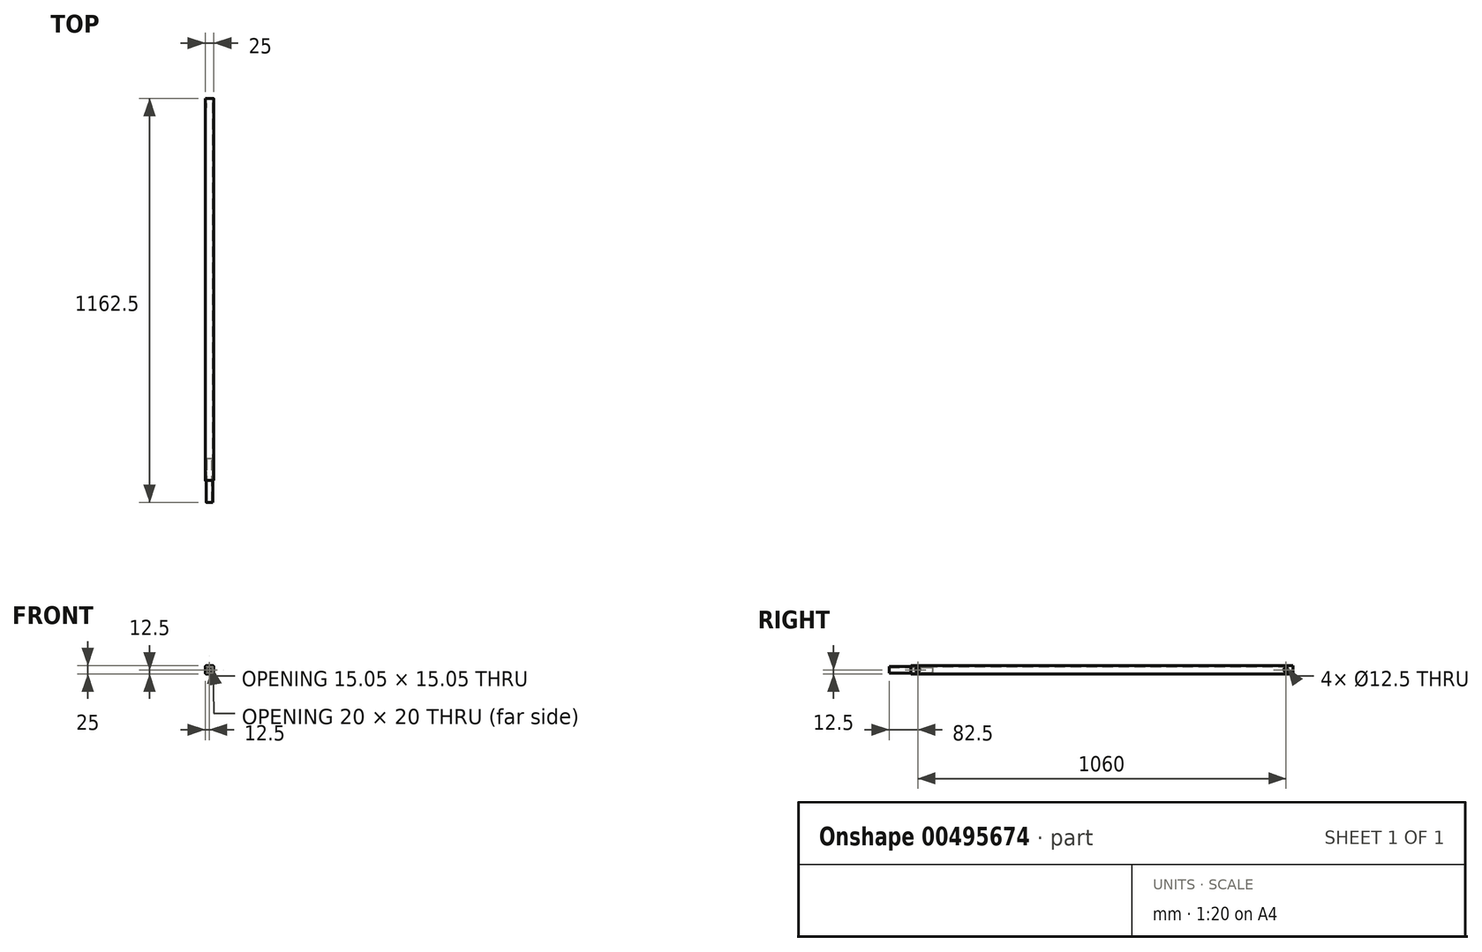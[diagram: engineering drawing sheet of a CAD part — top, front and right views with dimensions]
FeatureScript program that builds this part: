
annotation { "Feature Type Name" : "Feature", "Feature Type Description" : "" }
export const myFeature = defineFeature(function(context is Context, id is Id, definition is map)
    precondition{}
    {
        {
            var Q0;
            Q0=qCreatedBy(makeId("Front.planeOp"),FACE);
            var sketch = newSketch(context, id + "F0", { "sketchPlane" : qUnion([Q0])});
            skLineSegment(sketch, "E0.bottom", {"start": v(7.5, 12.5) * mm, "end": v(-7.5, 12.5) * mm});
            skLineSegment(sketch, "E0.top", {"start": v(7.5, -12.5) * mm, "end": v(-7.5, -12.5) * mm});
            skLineSegment(sketch, "E0.left", {"start": v(12.5, 7.5) * mm, "end": v(12.5, -7.5) * mm});
            skLineSegment(sketch, "E0.right", {"start": v(-12.5, 7.5) * mm, "end": v(-12.5, -7.5) * mm});
            skPoint(sketch, "E0.middle", {"position": v(0, 0) * mm});
            skPoint(sketch, "E1.visualSharp", {"position": v(-12.5, 12.5) * mm});
            skArc(sketch, "E1.filletArc", {"start": v(-7.5, 12.5) * mm, "mid": v(-11.04, 11.04) * mm, "end": v(-12.5, 7.5) * mm});
            skPoint(sketch, "E2.visualSharp", {"position": v(12.5, 12.5) * mm});
            skArc(sketch, "E2.filletArc", {"start": v(12.5, 7.5) * mm, "mid": v(11.04, 11.04) * mm, "end": v(7.5, 12.5) * mm});
            skPoint(sketch, "E3.visualSharp", {"position": v(12.5, -12.5) * mm});
            skArc(sketch, "E3.filletArc", {"start": v(7.5, -12.5) * mm, "mid": v(11.04, -11.04) * mm, "end": v(12.5, -7.5) * mm});
            skPoint(sketch, "E4.visualSharp", {"position": v(-12.5, -12.5) * mm});
            skArc(sketch, "E4.filletArc", {"start": v(-12.5, -7.5) * mm, "mid": v(-11.04, -11.04) * mm, "end": v(-7.5, -12.5) * mm});
            skLineSegment(sketch, "E5.0", {"start": v(7.5, 10) * mm, "end": v(-7.5, 10) * mm});
            skArc(sketch, "E5.1", {"start": v(10, 7.5) * mm, "mid": v(9.27, 9.27) * mm, "end": v(7.5, 10) * mm});
            skArc(sketch, "E5.2", {"start": v(-7.5, 10) * mm, "mid": v(-9.27, 9.27) * mm, "end": v(-10, 7.5) * mm});
            skLineSegment(sketch, "E5.3", {"start": v(10, 7.5) * mm, "end": v(10, -7.5) * mm});
            skLineSegment(sketch, "E5.4", {"start": v(-10, 7.5) * mm, "end": v(-10, -7.5) * mm});
            skArc(sketch, "E5.5", {"start": v(-10, -7.5) * mm, "mid": v(-9.27, -9.27) * mm, "end": v(-7.5, -10) * mm});
            skLineSegment(sketch, "E5.6", {"start": v(7.5, -10) * mm, "end": v(-7.5, -10) * mm});
            skArc(sketch, "E5.7", {"start": v(7.5, -10) * mm, "mid": v(9.27, -9.27) * mm, "end": v(10, -7.5) * mm});
            skSolve(sketch);
        }
        {
            var Q0;
            Q0=qSketchRegion(id+"F0",true);
            extrude(context, id + "F1", {"entities" : qUnion([Q0]), "endBound" : BoundingType.SYMMETRIC, "depth" : 1100 * mm});
        }
        {
            var Q0;
            Q0=makeQuery(id+"F1.opExtrude","SWEPT_FACE",FACE,{"disambiguationData":[OSD([sQuery(id+"F0.wireOp",EDGE,"E0.left")])]});
            var sketch = newSketch(context, id + "F2", { "sketchPlane" : qUnion([Q0])});
            skLineSegment(sketch, "E6", {"start": v(-550, 0) * mm, "end": v(-530, 0) * mm, "construction": true});
            skCircle(sketch, "E7", {"center": v(-530, 0) * mm, "radius": 6.25 * mm});
            skLineSegment(sketch, "E8", {"start": v(0, 0) * mm, "end": v(0, 13.57) * mm, "construction": true});
            skPoint(sketch, "E8.endSnap0", {"position": v(0, 7.5) * mm});
            skCircle(sketch, "E9.MirrorC", {"center": v(530, 0) * mm, "radius": 6.25 * mm});
            skSolve(sketch);
        }
        {
            var Q0;
            Q0=qSketchRegion(id+"F2",true);
            extrude(context, id + "F3", {"entities" : qUnion([Q0]), "operationType" : NewBodyOperationType.REMOVE, "endBound" : BoundingType.THROUGH_ALL, "oppositeDirection" : true, "depth" : 25 * mm});
        }
        {
            var Q0;
            Q0=makeQuery(id+"F1.opExtrude","CAP_FACE",FACE,{"disambiguationData":[OSD([sQuery(id+"F0.wireOp",EDGE,"E0.bottom"),sQuery(id+"F0.wireOp",EDGE,"E0.top"),sQuery(id+"F0.wireOp",EDGE,"E0.left"),sQuery(id+"F0.wireOp",EDGE,"E0.right"),sQuery(id+"F0.wireOp",EDGE,"E1.filletArc"),sQuery(id+"F0.wireOp",EDGE,"E2.filletArc"),sQuery(id+"F0.wireOp",EDGE,"E3.filletArc"),sQuery(id+"F0.wireOp",EDGE,"E4.filletArc"),sQuery(id+"F0.wireOp",EDGE,"E5.0"),sQuery(id+"F0.wireOp",EDGE,"E5.1"),sQuery(id+"F0.wireOp",EDGE,"E5.2"),sQuery(id+"F0.wireOp",EDGE,"E5.3"),sQuery(id+"F0.wireOp",EDGE,"E5.4"),sQuery(id+"F0.wireOp",EDGE,"E5.5"),sQuery(id+"F0.wireOp",EDGE,"E5.6"),sQuery(id+"F0.wireOp",EDGE,"E5.7")])],"isStart":false});
            var sketch = newSketch(context, id + "F4", { "sketchPlane" : qUnion([Q0])});
            skLineSegment(sketch, "E10.bottom", {"start": v(5.53, 9.53) * mm, "end": v(-5.53, 9.53) * mm});
            skLineSegment(sketch, "E10.top", {"start": v(5.53, -9.53) * mm, "end": v(-5.53, -9.53) * mm});
            skLineSegment(sketch, "E10.left", {"start": v(9.53, 5.53) * mm, "end": v(9.53, -5.53) * mm});
            skLineSegment(sketch, "E10.right", {"start": v(-9.53, 5.53) * mm, "end": v(-9.53, -5.53) * mm});
            skPoint(sketch, "E10.middle", {"position": v(0, 0) * mm});
            skPoint(sketch, "E11.visualSharp", {"position": v(-9.53, 9.53) * mm});
            skArc(sketch, "E11.filletArc", {"start": v(-5.53, 9.53) * mm, "mid": v(-8.35, 8.35) * mm, "end": v(-9.53, 5.53) * mm});
            skPoint(sketch, "E12.visualSharp", {"position": v(9.53, 9.53) * mm});
            skArc(sketch, "E12.filletArc", {"start": v(9.53, 5.53) * mm, "mid": v(8.35, 8.35) * mm, "end": v(5.53, 9.53) * mm});
            skPoint(sketch, "E13.visualSharp", {"position": v(9.53, -9.53) * mm});
            skArc(sketch, "E13.filletArc", {"start": v(5.53, -9.53) * mm, "mid": v(8.35, -8.35) * mm, "end": v(9.53, -5.53) * mm});
            skPoint(sketch, "E14.visualSharp", {"position": v(-9.53, -9.53) * mm});
            skArc(sketch, "E14.filletArc", {"start": v(-9.53, -5.53) * mm, "mid": v(-8.35, -8.35) * mm, "end": v(-5.53, -9.53) * mm});
            skArc(sketch, "E15.0", {"start": v(7.53, 5.53) * mm, "mid": v(6.94, 6.94) * mm, "end": v(5.53, 7.53) * mm});
            skLineSegment(sketch, "E15.1", {"start": v(7.53, 5.53) * mm, "end": v(7.53, -5.53) * mm});
            skLineSegment(sketch, "E15.2", {"start": v(5.53, 7.53) * mm, "end": v(-5.53, 7.53) * mm});
            skArc(sketch, "E15.3", {"start": v(5.53, -7.53) * mm, "mid": v(6.94, -6.94) * mm, "end": v(7.53, -5.53) * mm});
            skArc(sketch, "E15.4", {"start": v(-5.53, 7.53) * mm, "mid": v(-6.94, 6.94) * mm, "end": v(-7.53, 5.53) * mm});
            skLineSegment(sketch, "E15.5", {"start": v(-7.53, 5.53) * mm, "end": v(-7.53, -5.53) * mm});
            skArc(sketch, "E15.6", {"start": v(-7.53, -5.53) * mm, "mid": v(-6.94, -6.94) * mm, "end": v(-5.53, -7.53) * mm});
            skLineSegment(sketch, "E15.7", {"start": v(5.53, -7.53) * mm, "end": v(-5.53, -7.53) * mm});
            skSolve(sketch);
        }
        {
            var Q0;
            Q0 = qSketchRegion(id + "F4", true);
            extrude(context, id + "F5", {"entities" : qUnion([Q0]), "endBound" : BoundingType.SYMMETRIC, "depth" : 125 * mm});
        }
    });
